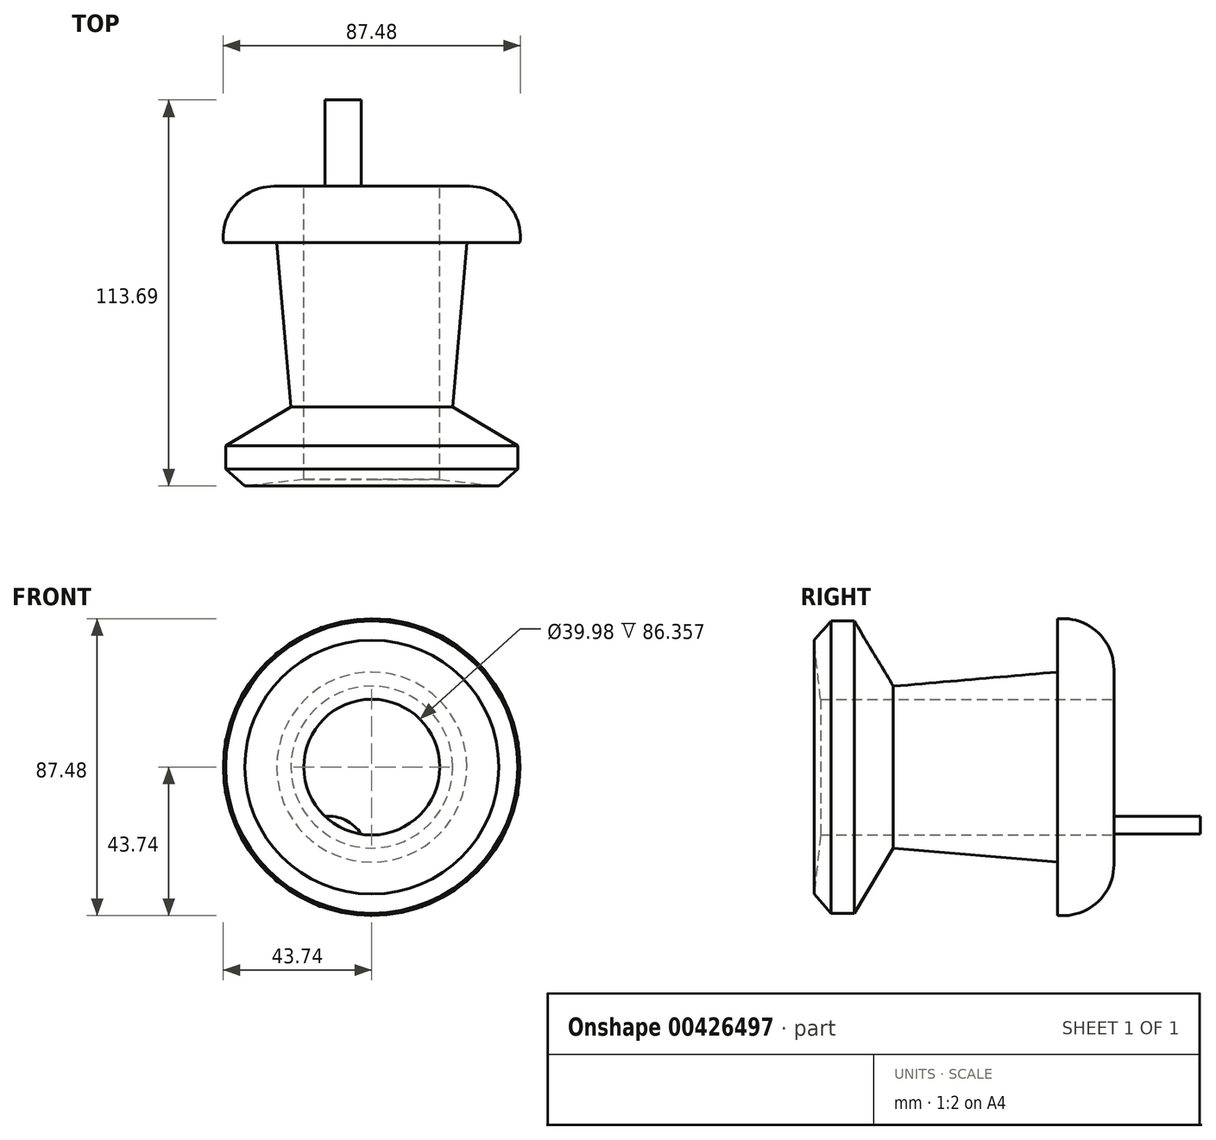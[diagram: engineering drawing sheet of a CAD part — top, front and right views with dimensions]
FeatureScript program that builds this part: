
annotation { "Feature Type Name" : "Feature", "Feature Type Description" : "" }
export const myFeature = defineFeature(function(context is Context, id is Id, definition is map)
    precondition{}
    {
        {
            var Q0;
            Q0=qCreatedBy(makeId("Top.planeOp"),FACE);
            var sketch = newSketch(context, id + "F0", { "sketchPlane" : qUnion([Q0])});
            skLineSegment(sketch, "E0", {"start": v(-20, 45.58) * mm, "end": v(-51.65, 45.58) * mm});
            skLineSegment(sketch, "E1", {"start": v(-51.65, 45.58) * mm, "end": v(-43.66, 28.95) * mm});
            skLineSegment(sketch, "E2", {"start": v(-43.66, 28.95) * mm, "end": v(-27.99, 28.95) * mm});
            skLineSegment(sketch, "E3", {"start": v(-27.99, 28.95) * mm, "end": v(-23.83, -19.35) * mm});
            skLineSegment(sketch, "E4", {"start": v(-23.83, -19.35) * mm, "end": v(-43.02, -30.86) * mm});
            skLineSegment(sketch, "E5", {"start": v(-43.02, -30.86) * mm, "end": v(-43.02, -43.34) * mm});
            skLineSegment(sketch, "E6", {"start": v(-43.02, -43.34) * mm, "end": v(-20, -40.78) * mm});
            skLineSegment(sketch, "E7", {"start": v(-20, -40.78) * mm, "end": v(-20, 45.58) * mm});
            skLineSegment(sketch, "E8", {"start": v(0, 43.66) * mm, "end": v(0, -46.22) * mm, "construction": true});
            skSolve(sketch);
        }
        {
            var Q0;
            Q0=makeQuery(id+"F0.imprint","IMPRINT",FACE,{"disambiguationData":[TD([[makeQuery(id+"F0.imprint","IMPRINT",EDGE,{"derivedFrom":sQuery(id+"F0.wireOp",EDGE,"E0")}),1.0]])]});
            var Q1;
            Q1=sQuery(id+"F0.wireOp",EDGE,"E8");
            revolve(context, id + "F1", {"entities" : qUnion([Q0]), "axis" : qUnion([Q1]), "revolveType" : RevolveType.FULL});
        }
        {
            var Q0;
            Q0=makeQuery(id+"F1.opRevolve","SWEPT_EDGE",EDGE,{"disambiguationData":[OSD([sQuery(id+"F0.wireOp",EDGE,"E0"),sQuery(id+"F0.wireOp",EDGE,"E1")])]});
            fillet(context, id + "F2", {"entities" : qUnion([Q0]), "radius" : 15.03 * mm, "tangentPropagation" : true, "allowEdgeOverflow" : false});
        }
        {
            var Q0;
            Q0=makeQuery(id+"F1.opRevolve","SWEPT_EDGE",EDGE,{"disambiguationData":[OSD([sQuery(id+"F0.wireOp",EDGE,"E5"),sQuery(id+"F0.wireOp",EDGE,"E6")])]});
            chamfer(context, id + "F3", {"entities" : qUnion([Q0]), "width" : 5.08 * mm, "tangentPropagation" : true});
        }
        {
            var Q0;
            Q0=makeQuery(id+"F1.opRevolve","SWEPT_FACE",FACE,{"disambiguationData":[OSD([sQuery(id+"F0.wireOp",EDGE,"E0")])]});
            var sketch = newSketch(context, id + "F4", { "sketchPlane" : qUnion([Q0])});
            skCircle(sketch, "E9", {"center": v(12.68, -25.76) * mm, "radius": 11.3 * mm});
            skSolve(sketch);
        }
        {
            var Q0;
            {var subQ0=sQuery(id+"F4.wireOp",EDGE,"E9");var subQ1=sQuery(id+"F0.wireOp",EDGE,"E0");var subQ4=makeQuery(id+"F1.opRevolve","SWEPT_EDGE",EDGE,{"disambiguationData":[OSD([subQ1,sQuery(id+"F0.wireOp",EDGE,"E7")])]});var subQ5=makeQuery(id+"F4.imprint","INTERSECT",VERTEX,{"disambiguationData":[OD(0.0)],"derivedFrom":[subQ4,subQ0]});Q0=makeQuery(id+"F4.imprint","IMPRINT",FACE,{"disambiguationData":[TD([[makeQuery(id+"F4.imprint","IMPRINT",EDGE,{"disambiguationData":[TD([[subQ5,1.0]])],"derivedFrom":subQ0}),1.0]])]});}
            var Q1;
            Q1=sQuery(id+"F4.wireOp",EDGE,"E9");
            extrude(context, id + "F5", {"entities" : qUnion([Q0]), "operationType" : NewBodyOperationType.ADD, "surfaceEntities" : qUnion([Q1]), "depth" : 25.4 * mm});
        }
    });
